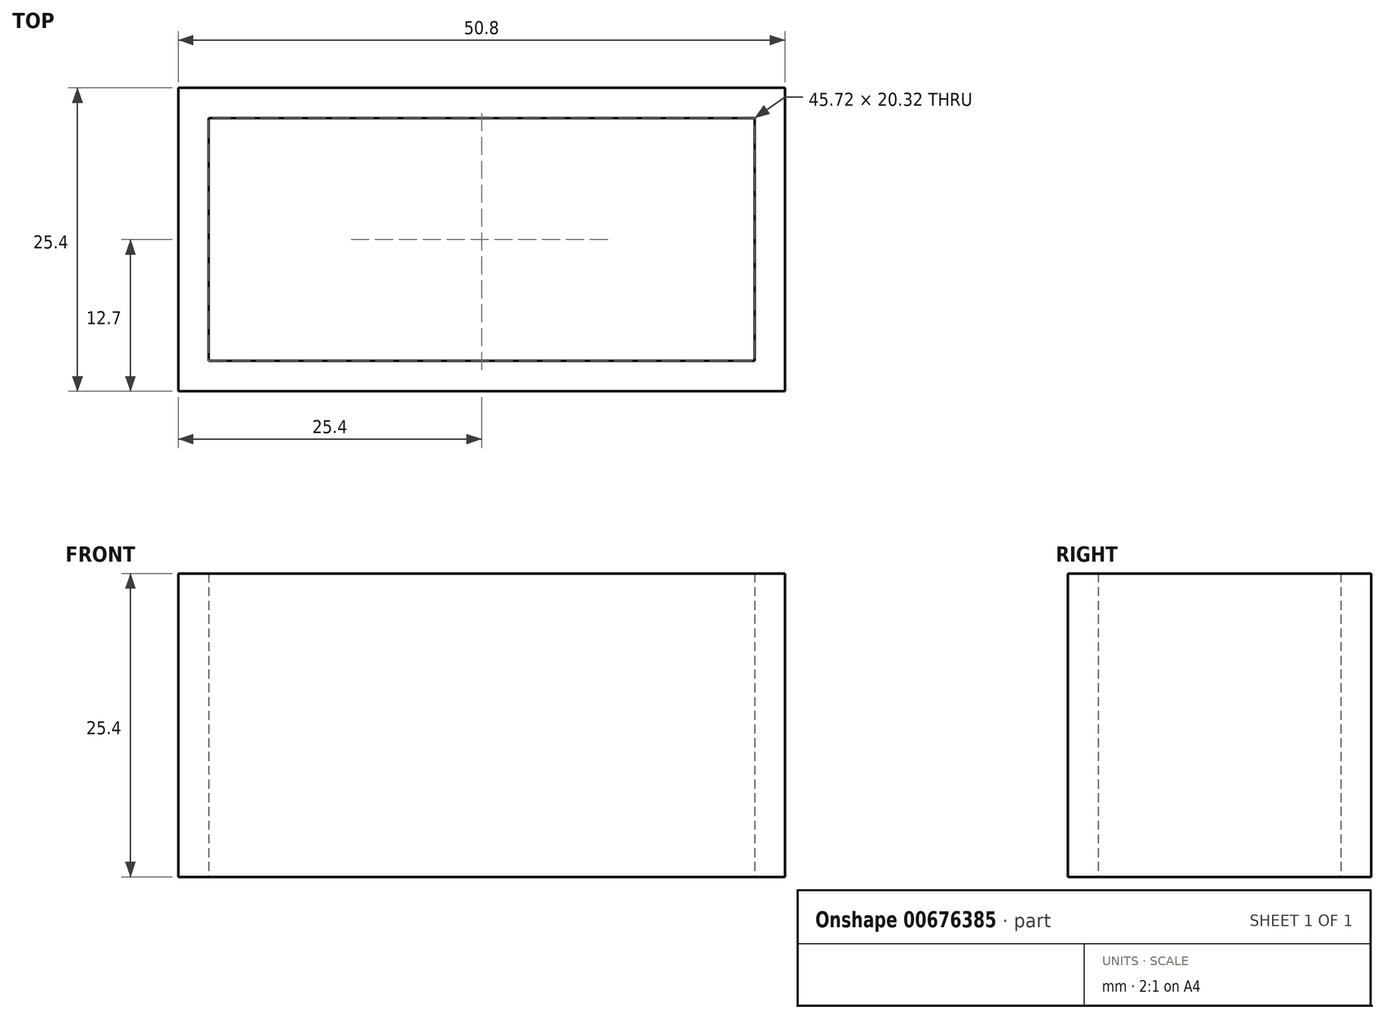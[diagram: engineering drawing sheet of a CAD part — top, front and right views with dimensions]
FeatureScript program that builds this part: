
annotation { "Feature Type Name" : "Feature", "Feature Type Description" : "" }
export const myFeature = defineFeature(function(context is Context, id is Id, definition is map)
    precondition{}
    {
        {
            var Q0;
            Q0=qCreatedBy(makeId("Top.planeOp"),FACE);
            var sketch = newSketch(context, id + "F0", { "sketchPlane" : qUnion([Q0])});
            skLineSegment(sketch, "E0.bottom", {"start": v(0, 0) * mm, "end": v(50.8, 0) * mm});
            skLineSegment(sketch, "E0.top", {"start": v(0, 25.4) * mm, "end": v(50.8, 25.4) * mm});
            skLineSegment(sketch, "E0.left", {"start": v(0, 0) * mm, "end": v(0, 25.4) * mm});
            skLineSegment(sketch, "E0.right", {"start": v(50.8, 0) * mm, "end": v(50.8, 25.4) * mm});
            skLineSegment(sketch, "E1", {"start": v(0, 12.7) * mm, "end": v(50.8, 12.7) * mm, "construction": true});
            skLineSegment(sketch, "E2", {"start": v(25.4, 25.4) * mm, "end": v(25.4, 0) * mm, "construction": true});
            skLineSegment(sketch, "E3", {"start": v(2.54, 12.7) * mm, "end": v(2.54, 22.86) * mm});
            skLineSegment(sketch, "E4", {"start": v(2.54, 22.86) * mm, "end": v(25.4, 22.86) * mm});
            skLineSegment(sketch, "E5.MirrorCS", {"start": v(48.26, 22.86) * mm, "end": v(25.4, 22.86) * mm});
            skLineSegment(sketch, "E6.MirrorCS", {"start": v(48.26, 12.7) * mm, "end": v(48.26, 22.86) * mm});
            skLineSegment(sketch, "E7.MirrorCS", {"start": v(2.54, 12.7) * mm, "end": v(2.54, 2.54) * mm});
            skLineSegment(sketch, "E8.MirrorCS", {"start": v(2.54, 2.54) * mm, "end": v(25.4, 2.54) * mm});
            skLineSegment(sketch, "E9.MirrorCS", {"start": v(48.26, 2.54) * mm, "end": v(25.4, 2.54) * mm});
            skLineSegment(sketch, "E10.MirrorCS", {"start": v(48.26, 12.7) * mm, "end": v(48.26, 2.54) * mm});
            skSolve(sketch);
        }
        {
            var Q0;
            Q0 = qSketchRegion(id + "F0", true);
            var Q1;
            Q1=makeQuery(id+"F0.imprint","IMPRINT",FACE,{"disambiguationData":[TD([[makeQuery(id+"F0.imprint","IMPRINT",EDGE,{"derivedFrom":sQuery(id+"F0.wireOp",EDGE,"E0.bottom")}),1.0]])]});
            extrude(context, id + "F1", {"entities" : qUnion([Q0, Q1]), "depth" : 25.4 * mm, "offsetDistance" : 25.4 * mm});
        }
    });
